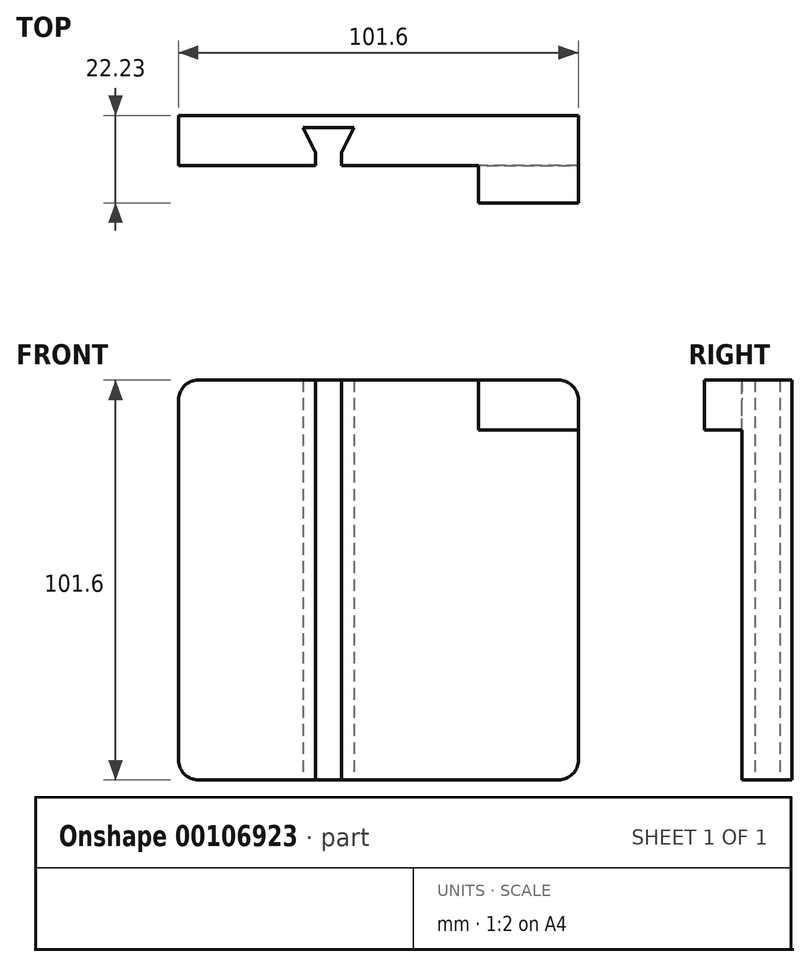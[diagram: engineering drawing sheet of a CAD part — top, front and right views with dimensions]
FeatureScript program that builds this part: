
annotation { "Feature Type Name" : "Feature", "Feature Type Description" : "" }
export const myFeature = defineFeature(function(context is Context, id is Id, definition is map)
    precondition{}
    {
        {
            var Q0;
            Q0=qCreatedBy(makeId("Front.planeOp"),FACE);
            var sketch = newSketch(context, id + "F0", { "sketchPlane" : qUnion([Q0])});
            skLineSegment(sketch, "E0.bottom", {"start": v(0, 0) * mm, "end": v(101.6, 0) * mm});
            skLineSegment(sketch, "E0.top", {"start": v(0, 101.6) * mm, "end": v(101.6, 101.6) * mm});
            skLineSegment(sketch, "E0.left", {"start": v(0, 0) * mm, "end": v(0, 101.6) * mm});
            skLineSegment(sketch, "E0.right", {"start": v(101.6, 0) * mm, "end": v(101.6, 101.6) * mm});
            skSolve(sketch);
        }
        {
            var Q0;
            Q0=makeQuery(id+"F0.imprint","IMPRINT",FACE,{"disambiguationData":[TD([[makeQuery(id+"F0.imprint","IMPRINT",EDGE,{"derivedFrom":sQuery(id+"F0.wireOp",EDGE,"E0.bottom")}),1.0]])]});
            extrude(context, id + "F1", {"entities" : qUnion([Q0]), "depth" : 12.7 * mm});
        }
        {
            var Q0;
            Q0=makeQuery(id+"F1.opExtrude","CAP_FACE",FACE,{"disambiguationData":[OSD([sQuery(id+"F0.wireOp",EDGE,"E0.bottom"),sQuery(id+"F0.wireOp",EDGE,"E0.top"),sQuery(id+"F0.wireOp",EDGE,"E0.left"),sQuery(id+"F0.wireOp",EDGE,"E0.right")])],"isStart":false});
            var sketch = newSketch(context, id + "F2", { "sketchPlane" : qUnion([Q0])});
            skLineSegment(sketch, "E1.bottom", {"start": v(101.6, 88.9) * mm, "end": v(76.2, 88.9) * mm});
            skLineSegment(sketch, "E1.top", {"start": v(101.6, 101.6) * mm, "end": v(76.2, 101.6) * mm});
            skLineSegment(sketch, "E1.left", {"start": v(101.6, 88.9) * mm, "end": v(101.6, 101.6) * mm});
            skLineSegment(sketch, "E1.right", {"start": v(76.2, 88.9) * mm, "end": v(76.2, 101.6) * mm});
            skSolve(sketch);
        }
        {
            var Q0;
            Q0=makeQuery(id+"F2.imprint","IMPRINT",FACE,{"disambiguationData":[TD([[makeQuery(id+"F2.imprint","IMPRINT",EDGE,{"derivedFrom":sQuery(id+"F2.wireOp",EDGE,"E1.bottom")}),-1.0]])]});
            extrude(context, id + "F3", {"entities" : qUnion([Q0]), "operationType" : NewBodyOperationType.ADD, "depth" : 9.52 * mm});
        }
        {
            var Q0;
            Q0=makeQuery(id+"F1.opExtrude","SWEPT_FACE",FACE,{"disambiguationData":[OSD([sQuery(id+"F0.wireOp",EDGE,"E0.bottom")])]});
            var sketch = newSketch(context, id + "F4", { "sketchPlane" : qUnion([Q0])});
            skLineSegment(sketch, "E2", {"start": v(38.1, 12.7) * mm, "end": v(38.1, 0) * mm});
            skLineSegment(sketch, "E3", {"start": v(38.1, 3.05) * mm, "end": v(31.62, 3.05) * mm});
            skLineSegment(sketch, "E4", {"start": v(38.1, 3.05) * mm, "end": v(44.58, 3.05) * mm});
            skLineSegment(sketch, "E5", {"start": v(34.8, 9.4) * mm, "end": v(31.62, 3.05) * mm});
            skLineSegment(sketch, "E6", {"start": v(44.58, 3.05) * mm, "end": v(41.4, 9.4) * mm});
            skLineSegment(sketch, "E7", {"start": v(41.4, 9.4) * mm, "end": v(41.4, 12.7) * mm});
            skLineSegment(sketch, "E8", {"start": v(34.8, 9.4) * mm, "end": v(34.8, 12.7) * mm});
            skLineSegment(sketch, "E9", {"start": v(34.8, 12.7) * mm, "end": v(41.4, 12.7) * mm});
            skPoint(sketch, "E10.start.orphan", {"position": v(38.1, 9.4) * mm});
            skSolve(sketch);
        }
        {
            var Q0;
            {var subQ0=sQuery(id+"F4.wireOp",EDGE,"E4");Q0=makeQuery(id+"F4.imprint","IMPRINT",FACE,{"disambiguationData":[TD([[makeQuery(id+"F4.imprint","IMPRINT",EDGE,{"derivedFrom":subQ0}),1.0]])]});}
            var Q1;
            {var subQ1=sQuery(id+"F4.wireOp",EDGE,"E3");Q1=makeQuery(id+"F4.imprint","IMPRINT",FACE,{"disambiguationData":[TD([[makeQuery(id+"F4.imprint","IMPRINT",EDGE,{"derivedFrom":subQ1}),-1.0]])]});}
            extrude(context, id + "F5", {"entities" : qUnion([Q0, Q1]), "operationType" : NewBodyOperationType.REMOVE, "endBound" : BoundingType.THROUGH_ALL, "oppositeDirection" : true, "depth" : 25.4 * mm});
        }
        {
            var Q0;
            Q0=makeQuery(id+"F1.opExtrude","SWEPT_EDGE",EDGE,{"disambiguationData":[OSD([sQuery(id+"F0.wireOp",EDGE,"E0.top"),sQuery(id+"F0.wireOp",EDGE,"E0.left")])]});
            var Q1;
            Q1=makeQuery(id+"F1.opExtrude","SWEPT_EDGE",EDGE,{"disambiguationData":[OSD([sQuery(id+"F0.wireOp",EDGE,"E0.bottom"),sQuery(id+"F0.wireOp",EDGE,"E0.left")])]});
            var Q2;
            Q2=makeQuery(id+"F1.opExtrude","SWEPT_EDGE",EDGE,{"disambiguationData":[OSD([sQuery(id+"F0.wireOp",EDGE,"E0.bottom"),sQuery(id+"F0.wireOp",EDGE,"E0.right")])]});
            var Q3;
            Q3=makeQuery(id+"F3.boolean.opBoolean","MERGE",EDGE,{"derivedFrom":[makeQuery(id+"F1.opExtrude","SWEPT_EDGE",EDGE,{"disambiguationData":[OSD([sQuery(id+"F0.wireOp",EDGE,"E0.top"),sQuery(id+"F0.wireOp",EDGE,"E0.right")])]}),makeQuery(id+"F3.opExtrude","SWEPT_EDGE",EDGE,{"disambiguationData":[OSD([sQuery(id+"F2.wireOp",EDGE,"E1.top"),sQuery(id+"F2.wireOp",EDGE,"E1.left")])]})]});
            fillet(context, id + "F6", {"entities" : qUnion([Q0, Q1, Q2, Q3]), "radius" : 5.08 * mm, "tangentPropagation" : true, "allowEdgeOverflow" : false});
        }
    });
